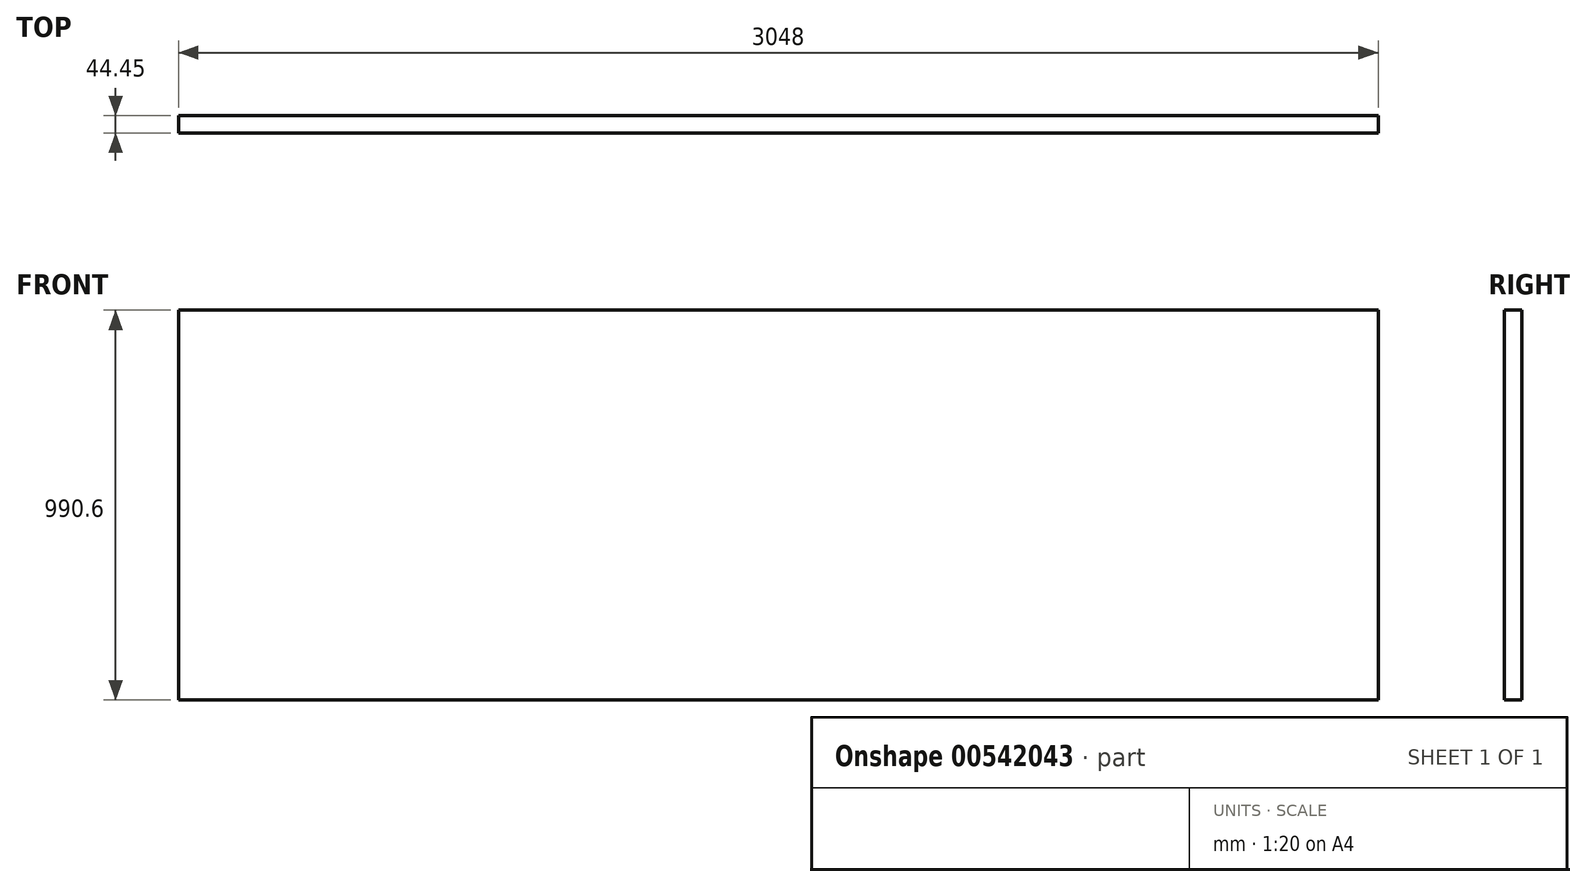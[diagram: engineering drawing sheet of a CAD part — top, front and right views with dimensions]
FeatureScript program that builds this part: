
annotation { "Feature Type Name" : "Feature", "Feature Type Description" : "" }
export const myFeature = defineFeature(function(context is Context, id is Id, definition is map)
    precondition{}
    {
        {
            var Q0;
            Q0=qCreatedBy(makeId("Front.planeOp"),FACE);
            var sketch = newSketch(context, id + "F0", { "sketchPlane" : qUnion([Q0])});
            skLineSegment(sketch, "E0.bottom", {"start": v(-1524, 495.3) * mm, "end": v(1524, 495.3) * mm});
            skLineSegment(sketch, "E0.top", {"start": v(-1524, -495.3) * mm, "end": v(1524, -495.3) * mm});
            skLineSegment(sketch, "E0.left", {"start": v(-1524, 495.3) * mm, "end": v(-1524, -495.3) * mm});
            skLineSegment(sketch, "E0.right", {"start": v(1524, 495.3) * mm, "end": v(1524, -495.3) * mm});
            skPoint(sketch, "E0.middle", {"position": v(0, 0) * mm});
            skSolve(sketch);
        }
        {
            var Q0;
            Q0=qSketchRegion(id+"F0",true);
            extrude(context, id + "F1", {"entities" : qUnion([Q0]), "depth" : 44.45 * mm, "offsetDistance" : 25.4 * mm});
        }
    });
